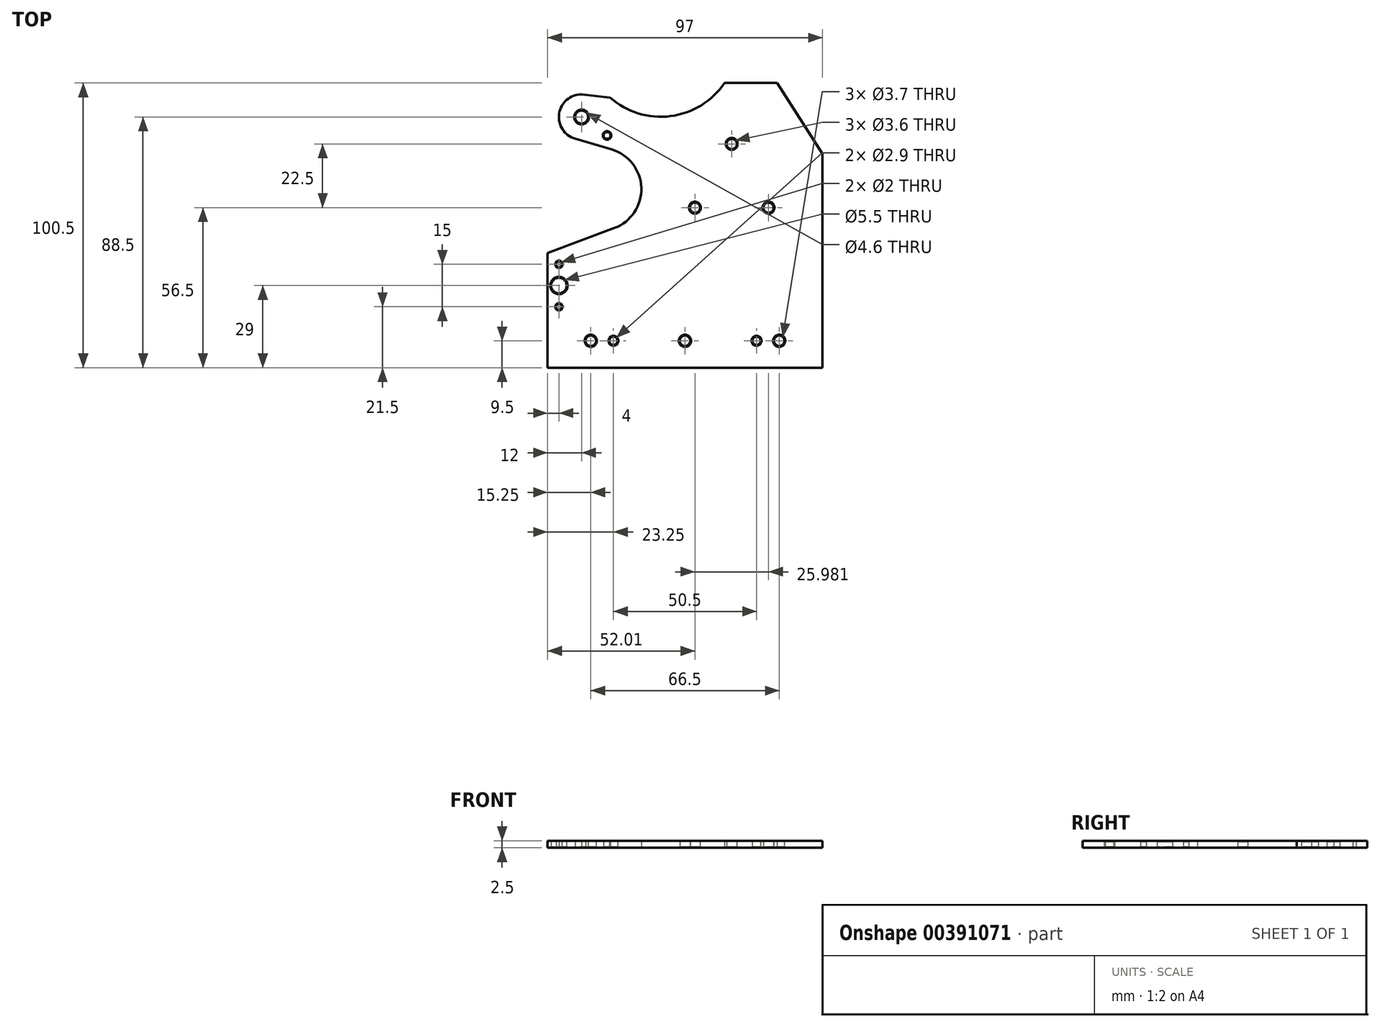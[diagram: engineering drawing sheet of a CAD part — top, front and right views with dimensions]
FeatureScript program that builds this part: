
annotation { "Feature Type Name" : "Feature", "Feature Type Description" : "" }
export const myFeature = defineFeature(function(context is Context, id is Id, definition is map)
    precondition{}
    {
        {
            var Q0;
            Q0=qCreatedBy(makeId("Top.planeOp"),FACE);
            var sketch = newSketch(context, id + "F0", { "sketchPlane" : qUnion([Q0])});
            skLineSegment(sketch, "E0.bottom", {"start": v(0, 0) * mm, "end": v(97, 0) * mm});
            skLineSegment(sketch, "E0.top", {"start": v(0, 100.5) * mm, "end": v(17.56, 100.5) * mm, "construction": true});
            skLineSegment(sketch, "E0.left", {"start": v(0, 0) * mm, "end": v(0, 100.5) * mm});
            skLineSegment(sketch, "E0.right", {"start": v(97, 0) * mm, "end": v(97, 75.5) * mm});
            skPoint(sketch, "E1", {"position": v(0, 40.5) * mm});
            skPoint(sketch, "E2", {"position": v(18.5, 63) * mm});
            skArc(sketch, "E3", {"start": v(23.61, 49.32) * mm, "mid": v(33.1, 63.5) * mm, "end": v(22.65, 77) * mm});
            skLineSegment(sketch, "E4", {"start": v(0, 40.5) * mm, "end": v(23.61, 49.32) * mm});
            skPoint(sketch, "E5", {"position": v(12, 88.5) * mm});
            skArc(sketch, "E6", {"start": v(13.75, 96.3) * mm, "mid": v(4.26, 90.51) * mm, "end": v(9.73, 80.83) * mm});
            skLineSegment(sketch, "E7", {"start": v(9.73, 80.83) * mm, "end": v(22.65, 77) * mm});
            skPoint(sketch, "E8", {"position": v(40, 115.7) * mm});
            skArc(sketch, "E9", {"start": v(22.06, 95.39) * mm, "mid": v(43.4, 88.81) * mm, "end": v(62.44, 100.5) * mm});
            skLineSegment(sketch, "E10", {"start": v(81, 100.5) * mm, "end": v(97, 75.5) * mm});
            skPoint(sketch, "E11.orphan", {"position": v(97, 100.5) * mm});
            skLineSegment(sketch, "E12.trimOffspring", {"start": v(62.44, 100.5) * mm, "end": v(81, 100.5) * mm});
            skPoint(sketch, "E13", {"position": v(12, 96.5) * mm});
            skLineSegment(sketch, "E14", {"start": v(12, 96.5) * mm, "end": v(22.06, 95.39) * mm});
            skCircle(sketch, "E15", {"center": v(12, 88.5) * mm, "radius": 2.3 * mm});
            skPoint(sketch, "E16", {"position": v(21, 82) * mm});
            skCircle(sketch, "E17", {"center": v(21, 82) * mm, "radius": 1.2 * mm});
            skPoint(sketch, "E18", {"position": v(65, 64) * mm});
            skCircle(sketch, "E19", {"center": v(65, 64) * mm, "radius": 15 * mm, "construction": true});
            skPoint(sketch, "E20", {"position": v(65, 79) * mm});
            skLineSegment(sketch, "E21", {"start": v(65, 64) * mm, "end": v(78, 56.5) * mm, "construction": true});
            skLineSegment(sketch, "E22", {"start": v(65, 64) * mm, "end": v(52, 56.5) * mm, "construction": true});
            skLineSegment(sketch, "E23", {"start": v(65, 64) * mm, "end": v(65, 79) * mm, "construction": true});
            skPoint(sketch, "E24", {"position": v(78, 56.5) * mm});
            skPoint(sketch, "E25", {"position": v(52, 56.5) * mm});
            skCircle(sketch, "E26", {"center": v(78, 56.5) * mm, "radius": 1.8 * mm});
            skCircle(sketch, "E27", {"center": v(65, 79) * mm, "radius": 1.8 * mm});
            skCircle(sketch, "E28", {"center": v(52, 56.5) * mm, "radius": 1.8 * mm});
            skPoint(sketch, "E29", {"position": v(4, 36.5) * mm});
            skPoint(sketch, "E30", {"position": v(4, 29) * mm});
            skPoint(sketch, "E31", {"position": v(4, 21.5) * mm});
            skCircle(sketch, "E32", {"center": v(4, 36.5) * mm, "radius": 1 * mm});
            skCircle(sketch, "E33", {"center": v(4, 21.5) * mm, "radius": 1 * mm});
            skCircle(sketch, "E34", {"center": v(4, 29) * mm, "radius": 2.75 * mm});
            skLineSegment(sketch, "E35", {"start": v(0, 9.5) * mm, "end": v(97, 9.5) * mm, "construction": true});
            skPoint(sketch, "E36", {"position": v(48.5, 9.5) * mm});
            skCircle(sketch, "E37", {"center": v(48.5, 9.5) * mm, "radius": 1.85 * mm});
            skPoint(sketch, "E38", {"position": v(23.25, 9.5) * mm});
            skPoint(sketch, "E39", {"position": v(73.75, 9.5) * mm});
            skCircle(sketch, "E40", {"center": v(73.75, 9.5) * mm, "radius": 1.45 * mm});
            skCircle(sketch, "E41", {"center": v(23.25, 9.5) * mm, "radius": 1.45 * mm});
            skPoint(sketch, "E42", {"position": v(81.75, 9.5) * mm});
            skPoint(sketch, "E43", {"position": v(15.25, 9.5) * mm});
            skCircle(sketch, "E44", {"center": v(81.75, 9.5) * mm, "radius": 1.85 * mm});
            skCircle(sketch, "E45", {"center": v(15.25, 9.5) * mm, "radius": 1.85 * mm});
            skSolve(sketch);
        }
        {
            var Q0;
            {var subQ0=sQuery(id+"F0.wireOp",EDGE,"E14");var subQ1=sQuery(id+"F0.wireOp",EDGE,"E6");var subQ2=makeQuery(id+"F0.imprint","INTERSECT",VERTEX,{"disambiguationData":[OD(0.0)],"derivedFrom":[subQ1,subQ0]});Q0=makeQuery(id+"F0.imprint","IMPRINT",FACE,{"disambiguationData":[TD([[makeQuery(id+"F0.imprint","IMPRINT",EDGE,{"disambiguationData":[TD([[subQ2,-1.0]])],"derivedFrom":subQ1}),1.0]])]});}
            var Q1;
            {var subQ6=sQuery(id+"F0.wireOp",EDGE,"E0.bottom");Q1=makeQuery(id+"F0.imprint","IMPRINT",FACE,{"disambiguationData":[TD([[makeQuery(id+"F0.imprint","IMPRINT",EDGE,{"derivedFrom":subQ6}),1.0]])]});}
            extrude(context, id + "F1", {"entities" : qUnion([Q0, Q1]), "depth" : 2.5 * mm, "offsetDistance" : 25 * mm});
        }
        {
            var Q0;
            Q0=makeQuery(id+"F1.opExtrude","CAP_EDGE",EDGE,{"disambiguationData":[OSD([sQuery(id+"F0.wireOp",EDGE,"E15")])],"isStart":false});
            var Q1;
            Q1=makeQuery(id+"F1.opExtrude","CAP_EDGE",EDGE,{"disambiguationData":[OSD([sQuery(id+"F0.wireOp",EDGE,"E17")])],"isStart":false});
            var Q2;
            Q2=makeQuery(id+"F1.opExtrude","CAP_EDGE",EDGE,{"disambiguationData":[OSD([sQuery(id+"F0.wireOp",EDGE,"E27")])],"isStart":false});
            var Q3;
            Q3=makeQuery(id+"F1.opExtrude","CAP_EDGE",EDGE,{"disambiguationData":[OSD([sQuery(id+"F0.wireOp",EDGE,"E28")])],"isStart":false});
            var Q4;
            Q4=makeQuery(id+"F1.opExtrude","CAP_EDGE",EDGE,{"disambiguationData":[OSD([sQuery(id+"F0.wireOp",EDGE,"E26")])],"isStart":false});
            var Q5;
            Q5=makeQuery(id+"F1.opExtrude","CAP_EDGE",EDGE,{"disambiguationData":[OSD([sQuery(id+"F0.wireOp",EDGE,"E32")])],"isStart":false});
            var Q6;
            Q6=makeQuery(id+"F1.opExtrude","CAP_EDGE",EDGE,{"disambiguationData":[OSD([sQuery(id+"F0.wireOp",EDGE,"E34")])],"isStart":false});
            var Q7;
            Q7=makeQuery(id+"F1.opExtrude","CAP_EDGE",EDGE,{"disambiguationData":[OSD([sQuery(id+"F0.wireOp",EDGE,"E33")])],"isStart":false});
            var Q8;
            Q8=makeQuery(id+"F1.opExtrude","CAP_EDGE",EDGE,{"disambiguationData":[OSD([sQuery(id+"F0.wireOp",EDGE,"E45")])],"isStart":false});
            var Q9;
            Q9=makeQuery(id+"F1.opExtrude","CAP_EDGE",EDGE,{"disambiguationData":[OSD([sQuery(id+"F0.wireOp",EDGE,"E41")])],"isStart":false});
            var Q10;
            Q10=makeQuery(id+"F1.opExtrude","CAP_EDGE",EDGE,{"disambiguationData":[OSD([sQuery(id+"F0.wireOp",EDGE,"E37")])],"isStart":false});
            var Q11;
            Q11=makeQuery(id+"F1.opExtrude","CAP_EDGE",EDGE,{"disambiguationData":[OSD([sQuery(id+"F0.wireOp",EDGE,"E40")])],"isStart":false});
            var Q12;
            Q12=makeQuery(id+"F1.opExtrude","CAP_EDGE",EDGE,{"disambiguationData":[OSD([sQuery(id+"F0.wireOp",EDGE,"E44")])],"isStart":false});
            var Q13;
            Q13=makeQuery(id+"F1.opExtrude","CAP_EDGE",EDGE,{"disambiguationData":[OSD([sQuery(id+"F0.wireOp",EDGE,"E45")])],"isStart":true});
            var Q14;
            Q14=makeQuery(id+"F1.opExtrude","CAP_EDGE",EDGE,{"disambiguationData":[OSD([sQuery(id+"F0.wireOp",EDGE,"E41")])],"isStart":true});
            var Q15;
            Q15=makeQuery(id+"F1.opExtrude","CAP_EDGE",EDGE,{"disambiguationData":[OSD([sQuery(id+"F0.wireOp",EDGE,"E37")])],"isStart":true});
            var Q16;
            Q16=makeQuery(id+"F1.opExtrude","CAP_EDGE",EDGE,{"disambiguationData":[OSD([sQuery(id+"F0.wireOp",EDGE,"E40")])],"isStart":true});
            var Q17;
            Q17=makeQuery(id+"F1.opExtrude","CAP_EDGE",EDGE,{"disambiguationData":[OSD([sQuery(id+"F0.wireOp",EDGE,"E44")])],"isStart":true});
            var Q18;
            Q18=makeQuery(id+"F1.opExtrude","CAP_EDGE",EDGE,{"disambiguationData":[OSD([sQuery(id+"F0.wireOp",EDGE,"E26")])],"isStart":true});
            var Q19;
            Q19=makeQuery(id+"F1.opExtrude","CAP_EDGE",EDGE,{"disambiguationData":[OSD([sQuery(id+"F0.wireOp",EDGE,"E28")])],"isStart":true});
            var Q20;
            Q20=makeQuery(id+"F1.opExtrude","CAP_EDGE",EDGE,{"disambiguationData":[OSD([sQuery(id+"F0.wireOp",EDGE,"E17")])],"isStart":true});
            var Q21;
            Q21=makeQuery(id+"F1.opExtrude","CAP_EDGE",EDGE,{"disambiguationData":[OSD([sQuery(id+"F0.wireOp",EDGE,"E15")])],"isStart":true});
            var Q22;
            Q22=makeQuery(id+"F1.opExtrude","CAP_EDGE",EDGE,{"disambiguationData":[OSD([sQuery(id+"F0.wireOp",EDGE,"E27")])],"isStart":true});
            var Q23;
            Q23=makeQuery(id+"F1.opExtrude","CAP_EDGE",EDGE,{"disambiguationData":[OSD([sQuery(id+"F0.wireOp",EDGE,"E33")])],"isStart":true});
            var Q24;
            Q24=makeQuery(id+"F1.opExtrude","CAP_EDGE",EDGE,{"disambiguationData":[OSD([sQuery(id+"F0.wireOp",EDGE,"E34")])],"isStart":true});
            var Q25;
            Q25=makeQuery(id+"F1.opExtrude","CAP_EDGE",EDGE,{"disambiguationData":[OSD([sQuery(id+"F0.wireOp",EDGE,"E32")])],"isStart":true});
            chamfer(context, id + "F2", {"entities" : qUnion([Q0, Q1, Q2, Q3, Q4, Q5, Q6, Q7, Q8, Q9, Q10, Q11, Q12, Q13, Q14, Q15, Q16, Q17, Q18, Q19, Q20, Q21, Q22, Q23, Q24, Q25]), "width" : .3 * mm, "tangentPropagation" : true});
        }
    });
